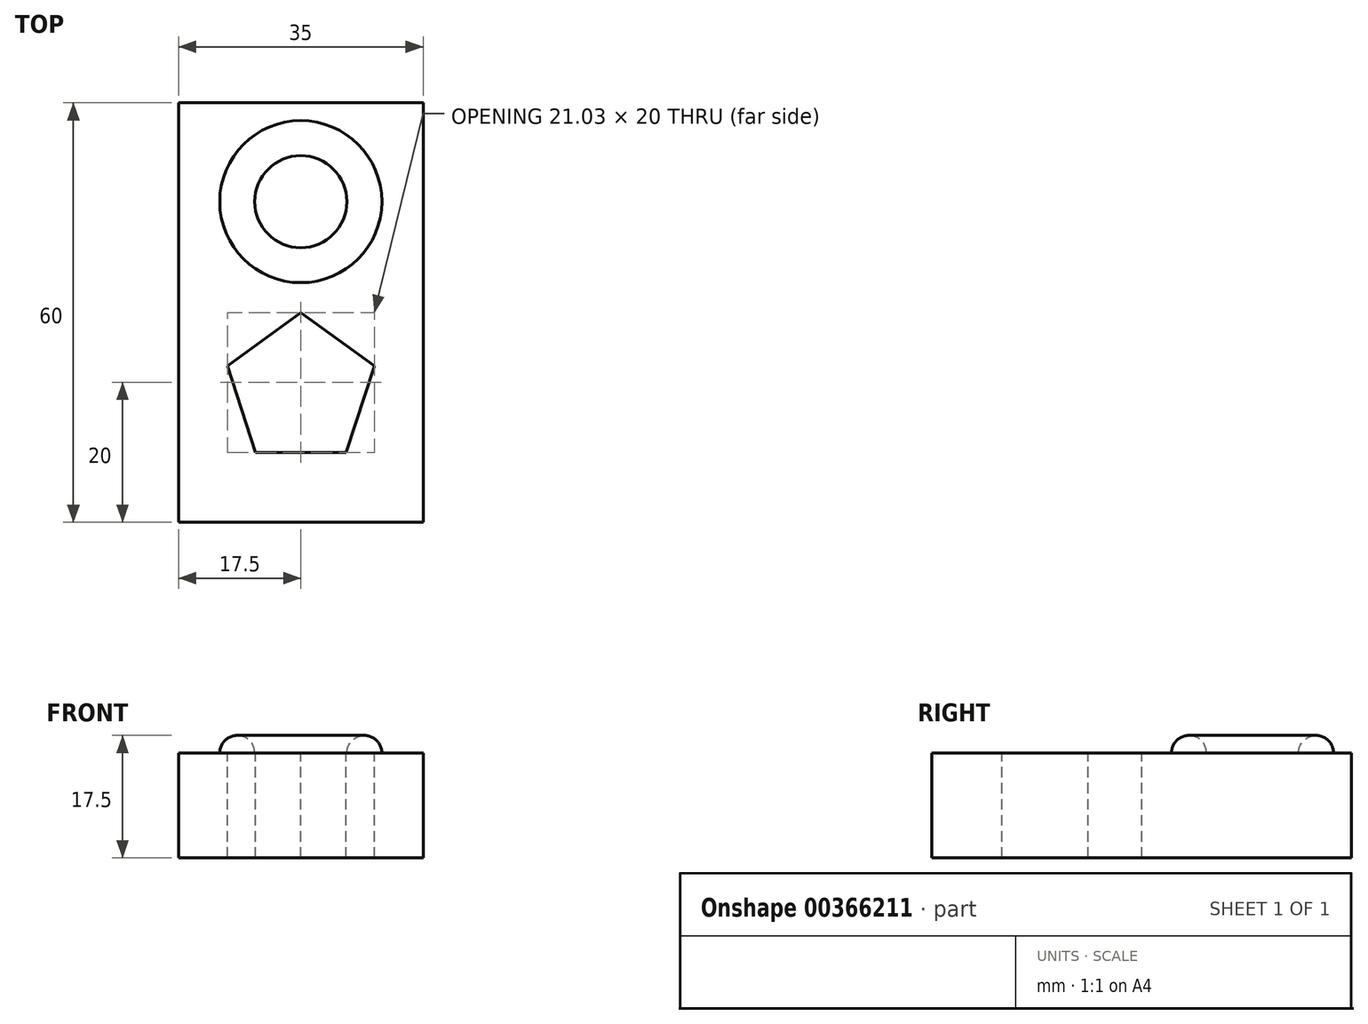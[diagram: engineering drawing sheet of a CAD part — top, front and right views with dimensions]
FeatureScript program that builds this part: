
annotation { "Feature Type Name" : "Feature", "Feature Type Description" : "" }
export const myFeature = defineFeature(function(context is Context, id is Id, definition is map)
    precondition{}
    {
        {
            var Q0;
            Q0=qCreatedBy(makeId("Top.planeOp"),FACE);
            var sketch = newSketch(context, id + "F0", { "sketchPlane" : qUnion([Q0])});
            skLineSegment(sketch, "E0.bottom", {"start": v(0, 0) * mm, "end": v(35, 0) * mm});
            skLineSegment(sketch, "E0.top", {"start": v(0, 60) * mm, "end": v(35, 60) * mm});
            skLineSegment(sketch, "E0.left", {"start": v(0, 0) * mm, "end": v(0, 60) * mm});
            skLineSegment(sketch, "E0.right", {"start": v(35, 0) * mm, "end": v(35, 60) * mm});
            skSolve(sketch);
        }
        {
            var Q0;
            Q0=makeQuery(id+"F0.imprint","IMPRINT",FACE,{"disambiguationData":[TD([[makeQuery(id+"F0.imprint","IMPRINT",EDGE,{"derivedFrom":sQuery(id+"F0.wireOp",EDGE,"E0.bottom")}),1.0]])]});
            extrude(context, id + "F1", {"entities" : qUnion([Q0]), "depth" : 15 * mm});
        }
        {
            var Q0;
            Q0=makeQuery(id+"F1.opExtrude","CAP_FACE",FACE,{"disambiguationData":[OSD([sQuery(id+"F0.wireOp",EDGE,"E0.bottom"),sQuery(id+"F0.wireOp",EDGE,"E0.top"),sQuery(id+"F0.wireOp",EDGE,"E0.left"),sQuery(id+"F0.wireOp",EDGE,"E0.right")])],"isStart":false});
            var sketch = newSketch(context, id + "F2", { "sketchPlane" : qUnion([Q0])});
            skCircle(sketch, "E1.cCircle", {"center": v(17.5, 18.94) * mm, "radius": 8.94 * mm, "construction": true});
            skLineSegment(sketch, "E1.0", {"start": v(28.01, 22.36) * mm, "end": v(24, 10) * mm});
            skLineSegment(sketch, "E1.1", {"start": v(24, 10) * mm, "end": v(11, 10) * mm});
            skLineSegment(sketch, "E1.2", {"start": v(11, 10) * mm, "end": v(6.99, 22.36) * mm});
            skLineSegment(sketch, "E1.3", {"start": v(6.99, 22.36) * mm, "end": v(17.5, 30) * mm});
            skLineSegment(sketch, "E1.4", {"start": v(17.5, 30) * mm, "end": v(28.01, 22.36) * mm});
            skPoint(sketch, "E1.0.midPoint", {"position": v(26, 16.18) * mm});
            skPoint(sketch, "E2", {"position": v(17.5, 0) * mm});
            skSolve(sketch);
        }
        {
            var Q0;
            Q0=makeQuery(id+"F2.imprint","IMPRINT",FACE,{"disambiguationData":[TD([[makeQuery(id+"F2.imprint","IMPRINT",EDGE,{"derivedFrom":sQuery(id+"F2.wireOp",EDGE,"E1.0")}),-1.0]])]});
            extrude(context, id + "F3", {"entities" : qUnion([Q0]), "operationType" : NewBodyOperationType.REMOVE, "oppositeDirection" : true, "depth" : 25 * mm});
        }
        {
            var Q0;
            Q0=makeQuery(id+"F1.opExtrude","SWEPT_FACE",FACE,{"disambiguationData":[OSD([sQuery(id+"F0.wireOp",EDGE,"E0.right")])]});
            var Q1;
            Q1=makeQuery(id+"F1.opExtrude","SWEPT_FACE",FACE,{"disambiguationData":[OSD([sQuery(id+"F0.wireOp",EDGE,"E0.left")])]});
            cPlane(context, id + "F4", {"entities" : qUnion([Q0, Q1]), "cplaneType" : CPlaneType.MID_PLANE, "offset" : 25 * mm, "oppositeDirection" : true, "width" : 150 * mm, "height" : 150 * mm});
        }
        {
            var Q0;
            Q0=qCreatedBy(id+"F4.planeOp",FACE);
            var sketch = newSketch(context, id + "F5", { "sketchPlane" : qUnion([Q0])});
            skCircle(sketch, "E3", {"center": v(36.76, 15) * mm, "radius": 2.5 * mm});
            skLineSegment(sketch, "E4.0", {"start": v(0, 15) * mm, "end": v(60, 15) * mm});
            skLineSegment(sketch, "E5", {"start": v(45.85, 15) * mm, "end": v(45.85, 22.66) * mm, "construction": true});
            skSolve(sketch);
        }
        {
            var Q0;
            {var subQ0=sQuery(id+"F5.wireOp",EDGE,"E4.0");var subQ1=sQuery(id+"F5.wireOp",EDGE,"E3");var subQ2=makeQuery(id+"F5.imprint","INTERSECT",VERTEX,{"disambiguationData":[OD(0.0)],"derivedFrom":[subQ1,subQ0]});Q0=makeQuery(id+"F5.imprint","IMPRINT",FACE,{"disambiguationData":[TD([[makeQuery(id+"F5.imprint","IMPRINT",EDGE,{"disambiguationData":[TD([[subQ2,1.0]])],"derivedFrom":subQ1}),1.0]])]});}
            var Q1;
            Q1=sQuery(id+"F5.wireOp",EDGE,"E5");
            revolve(context, id + "F6", {"operationType" : NewBodyOperationType.ADD, "entities" : qUnion([Q0]), "axis" : qUnion([Q1]), "revolveType" : RevolveType.FULL});
        }
    });
